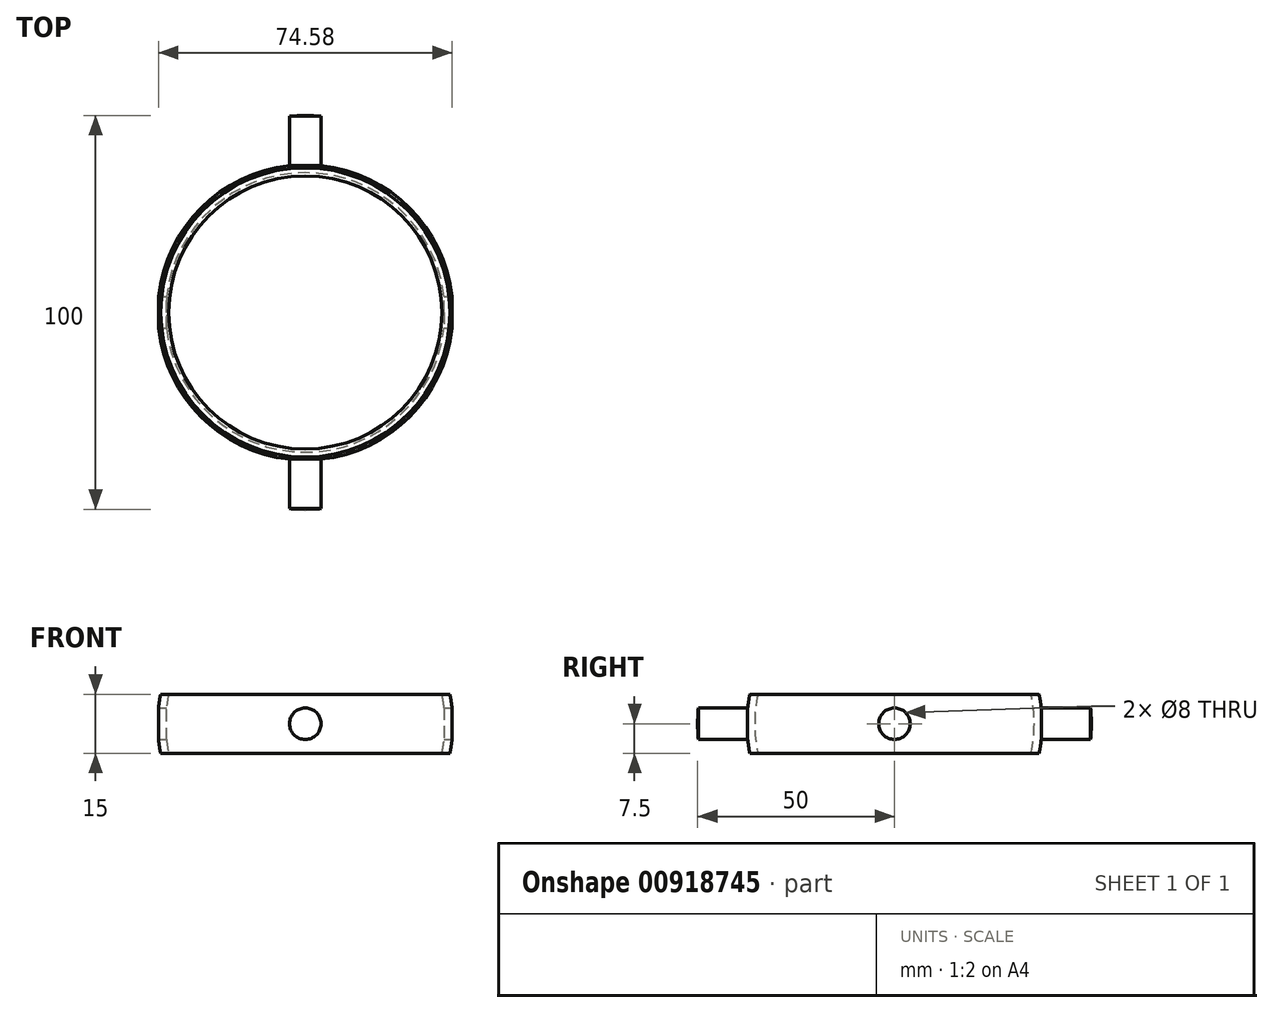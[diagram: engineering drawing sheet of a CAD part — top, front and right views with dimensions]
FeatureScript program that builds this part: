
annotation { "Feature Type Name" : "Feature", "Feature Type Description" : "" }
export const myFeature = defineFeature(function(context is Context, id is Id, definition is map)
    precondition{}
    {
        {
            var Q0;
            Q0=qCreatedBy(makeId("Front.planeOp"),FACE);
            var sketch = newSketch(context, id + "F0", { "sketchPlane" : qUnion([Q0])});
            skLineSegment(sketch, "E0", {"start": v(0, 33.72) * mm, "end": v(0, 0) * mm, "construction": true});
            skLineSegment(sketch, "E1", {"start": v(0, 0) * mm, "end": v(-39.15, 0) * mm, "construction": true});
            skArc(sketch, "E2", {"start": v(-36.74, 7.5) * mm, "mid": v(-37.5, 0) * mm, "end": v(-36.74, -7.5) * mm});
            skArc(sketch, "E3", {"start": v(-34.7, 7.5) * mm, "mid": v(-35.5, 0) * mm, "end": v(-34.7, -7.5) * mm});
            skLineSegment(sketch, "E4", {"start": v(-36.74, 7.5) * mm, "end": v(-34.7, 7.5) * mm});
            skLineSegment(sketch, "E5", {"start": v(-36.74, -7.5) * mm, "end": v(-34.7, -7.5) * mm});
            skSolve(sketch);
        }
        {
            var Q0;
            Q0 = qSketchRegion(id + "F0", true);
            var Q1;
            Q1=sQuery(id+"F0.wireOp",EDGE,"E0");
            revolve(context, id + "F1", {"surfaceOperationType" : NewSurfaceOperationType.NEW, "entities" : qUnion([Q0]), "axis" : qUnion([Q1]), "revolveType" : RevolveType.FULL});
        }
        {
            var Q0;
            Q0=qCreatedBy(makeId("Right.planeOp"),FACE);
            var sketch = newSketch(context, id + "F2", { "sketchPlane" : qUnion([Q0])});
            skCircle(sketch, "E6", {"center": v(0, 0) * mm, "radius": 4 * mm});
            skSolve(sketch);
        }
        {
            var Q0;
            Q0 = qSketchRegion(id + "F2", true);
            extrude(context, id + "F3", {"entities" : qUnion([Q0]), "operationType" : NewBodyOperationType.REMOVE, "endBound" : BoundingType.THROUGH_ALL, "oppositeDirection" : true, "depth" : 25.4 * mm, "offsetDistance" : 25.4 * mm, "hasSecondDirection" : true, "secondDirectionBound" : SecondDirectionBoundingType.THROUGH_ALL, "secondDirectionOppositeDirection" : false, "secondDirectionDepth" : 25.4 * mm});
        }
        {
            var Q0;
            Q0=qCreatedBy(makeId("Front.planeOp"),FACE);
            cPlane(context, id + "F4", {"entities" : qUnion([Q0]), "cplaneType" : CPlaneType.OFFSET, "offset" : 50 * mm, "width" : 152.4 * mm, "height" : 152.4 * mm});
        }
        {
            var Q0;
            Q0=qCreatedBy(id+"F4.planeOp",FACE);
            var sketch = newSketch(context, id + "F5", { "sketchPlane" : qUnion([Q0])});
            skCircle(sketch, "E7", {"center": v(0, 0) * mm, "radius": 4 * mm});
            skSolve(sketch);
        }
        {
            var Q0;
            Q0 = qSketchRegion(id + "F5", true);
            var Q1;
            Q1=makeQuery(id+"F1.opRevolve","SWEPT_FACE",FACE,{"disambiguationData":[OSD([sQuery(id+"F0.wireOp",EDGE,"E2")])]});
            extrude(context, id + "F6", {"entities" : qUnion([Q0]), "operationType" : NewBodyOperationType.ADD, "endBound" : BoundingType.UP_TO_SURFACE, "oppositeDirection" : true, "depth" : 25.4 * mm, "endBoundEntityFace" : qUnion([Q1]), "offsetDistance" : 25.4 * mm});
        }
        {
            var Q0;
            Q0=makeQuery(id+"F1.opRevolve","SWEPT_BODY",BODY,{"disambiguationData":[OSD([sQuery(id+"F0.wireOp",EDGE,"E2"),sQuery(id+"F0.wireOp",EDGE,"E3"),sQuery(id+"F0.wireOp",EDGE,"E4"),sQuery(id+"F0.wireOp",EDGE,"E5")])]});
            var Q1;
            Q1=qCreatedBy(makeId("Front.planeOp"),FACE);
            mirror(context, id + "F7", {"operationType" : NewBodyOperationType.ADD, "entities" : qUnion([Q0]), "mirrorPlane" : qUnion([Q1])});
        }
        {
            var Q0;
            Q0=qCreatedBy(makeId("Right.planeOp"),FACE);
            var sketch = newSketch(context, id + "F8", { "sketchPlane" : qUnion([Q0])});
            skLineSegment(sketch, "E8", {"start": v(0, 55) * mm, "end": v(0, 0) * mm, "construction": true});
            skLineSegment(sketch, "E9", {"start": v(0, 0) * mm, "end": v(-67.32, 0) * mm, "construction": true});
            skArc(sketch, "E10", {"start": v(0, 55) * mm, "mid": v(-55, 0) * mm, "end": v(0, -55) * mm});
            skArc(sketch, "E11", {"start": v(0, 50) * mm, "mid": v(-50, 0) * mm, "end": v(0, -50) * mm});
            skLineSegment(sketch, "E12", {"start": v(0, 55) * mm, "end": v(0, 50) * mm});
            skLineSegment(sketch, "E13", {"start": v(0, -50) * mm, "end": v(0, -55) * mm});
            skSolve(sketch);
        }
        {
            var Q0;
            Q0 = qSketchRegion(id + "F8", true);
            var Q1;
            Q1=sQuery(id+"F8.wireOp",EDGE,"E8");
            revolve(context, id + "F9", {"operationType" : NewBodyOperationType.REMOVE, "surfaceOperationType" : NewSurfaceOperationType.NEW, "entities" : qUnion([Q0]), "axis" : qUnion([Q1]), "revolveType" : RevolveType.FULL, "oppositeDirection" : true});
        }
    });
